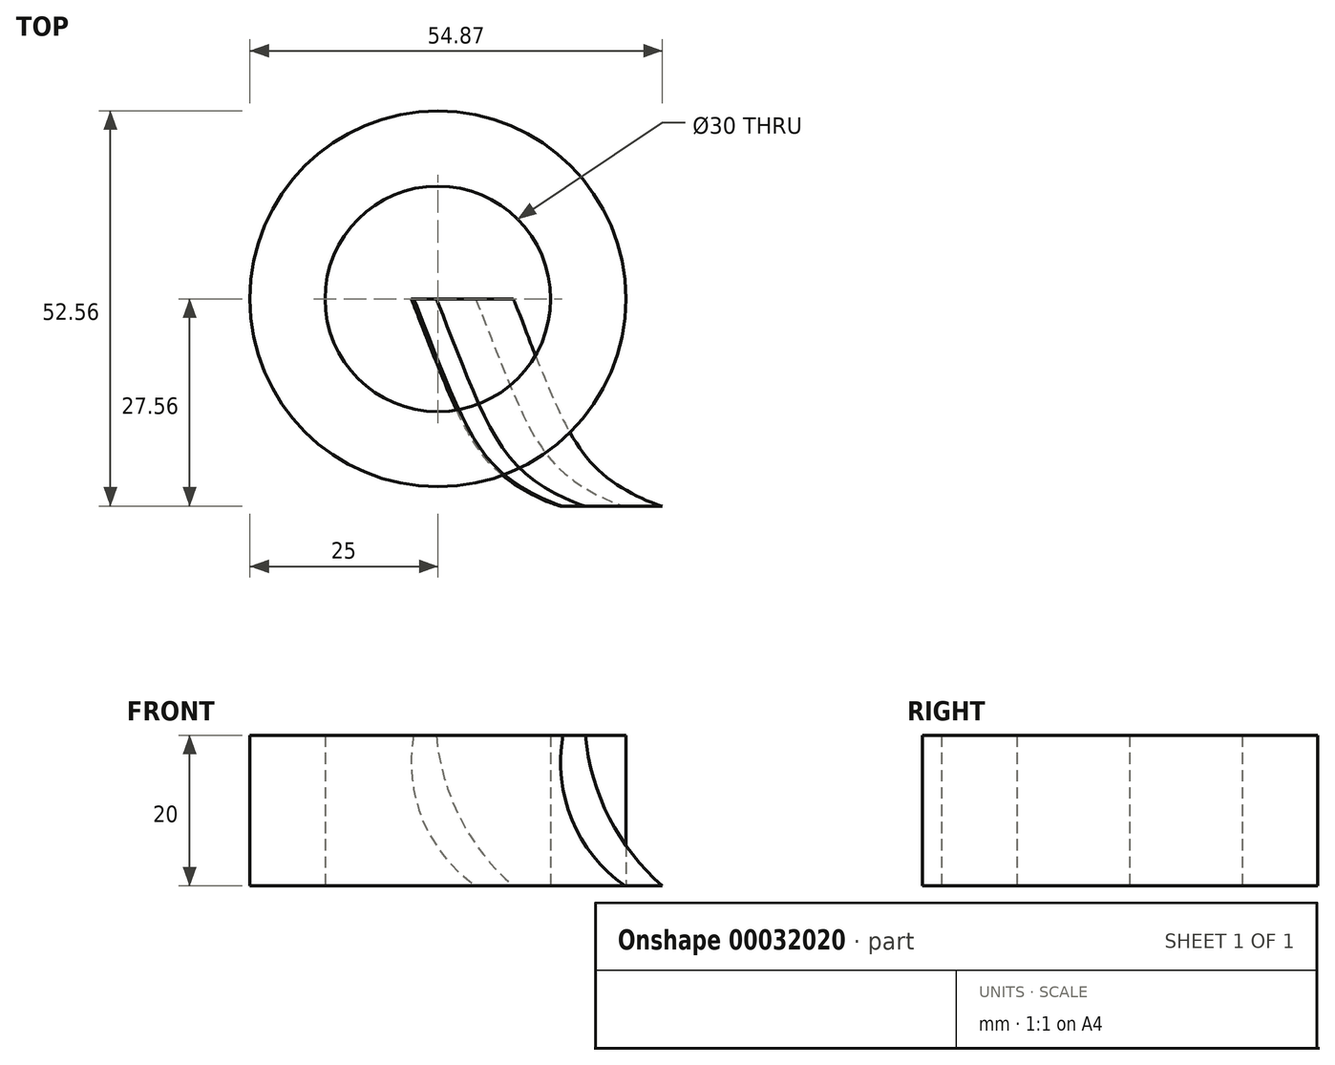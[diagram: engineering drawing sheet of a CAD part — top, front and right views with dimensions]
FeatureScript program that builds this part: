
annotation { "Feature Type Name" : "Feature", "Feature Type Description" : "" }
export const myFeature = defineFeature(function(context is Context, id is Id, definition is map)
    precondition{}
    {
        {
            var Q0;
            Q0=qCreatedBy(makeId("Top.planeOp"),FACE);
            var sketch = newSketch(context, id + "F0", { "sketchPlane" : qUnion([Q0])});
            skCircle(sketch, "E0", {"center": v(0, 0) * mm, "radius": 25 * mm});
            skCircle(sketch, "E1", {"center": v(0, 0) * mm, "radius": 15 * mm});
            skSolve(sketch);
        }
        {
            var Q0;
            Q0=makeQuery(id+"F0.imprint","IMPRINT",FACE,{"disambiguationData":[TD([[makeQuery(id+"F0.imprint","IMPRINT",EDGE,{"derivedFrom":sQuery(id+"F0.wireOp",EDGE,"E0")}),1.0]])]});
            extrude(context, id + "F1", {"entities" : qUnion([Q0]), "endBound" : BoundingType.SYMMETRIC, "depth" : 20 * mm});
        }
        {
            var Q0;
            Q0=qCreatedBy(makeId("Front.planeOp"),FACE);
            var sketch = newSketch(context, id + "F2", { "sketchPlane" : qUnion([Q0])});
            skLineSegment(sketch, "E2.0", {"start": v(-25, 10) * mm, "end": v(25, 10) * mm});
            skLineSegment(sketch, "E3.1", {"start": v(-25, -10) * mm, "end": v(25, -10) * mm});
            skArc(sketch, "E4", {"start": v(-0.2, 10) * mm, "mid": v(2.97, -1) * mm, "end": v(10.02, -10) * mm});
            skArc(sketch, "E5", {"start": v(-3.2, 10) * mm, "mid": v(-2.03, -1.2) * mm, "end": v(5.02, -10) * mm});
            skLineSegment(sketch, "E6", {"start": v(0, 0) * mm, "end": v(-2.48, 0) * mm, "construction": true});
            skLineSegment(sketch, "E7", {"start": v(0, 0) * mm, "end": v(2.48, 0) * mm, "construction": true});
            skSolve(sketch);
        }
        {
            var Q0;
            Q0=qCreatedBy(makeId("Top.planeOp"),FACE);
            var sketch = newSketch(context, id + "F3", { "sketchPlane" : qUnion([Q0])});
            skLineSegment(sketch, "E8.0", {"start": v(-25, 0) * mm, "end": v(25, 0) * mm});
            skFitSpline(sketch, "E9", {"points": [v(0, 0) * mm, v(5.17, -12.88) * mm, v(12.51, -23.79) * mm, v(19.85, -27.56) * mm], "startDerivative": vector(8.3, -19.24) * mm, "endDerivative": vector(11.49, -2.33) * mm});
            skSolve(sketch);
        }
        {
            var Q0;
            {var subQ1=sQuery(id+"F2.wireOp",EDGE,"E4");Q0=makeQuery(id+"F2.imprint","IMPRINT",FACE,{"disambiguationData":[TD([[makeQuery(id+"F2.imprint","IMPRINT",EDGE,{"derivedFrom":subQ1}),-1.0]])]});}
            var Q1;
            Q1=sQuery(id+"F2.wireOp",EDGE,"E5");
            var Q2;
            Q2=sQuery(id+"F2.wireOp",EDGE,"E4");
            var Q3;
            Q3=sQuery(id+"F3.wireOp",EDGE,"E9");
            sweep(context, id + "F4", {"profiles" : qUnion([Q0]), "surfaceProfiles" : qUnion([Q1, Q2]), "path" : qUnion([Q3]), "keepProfileOrientation" : true});
        }
    });
